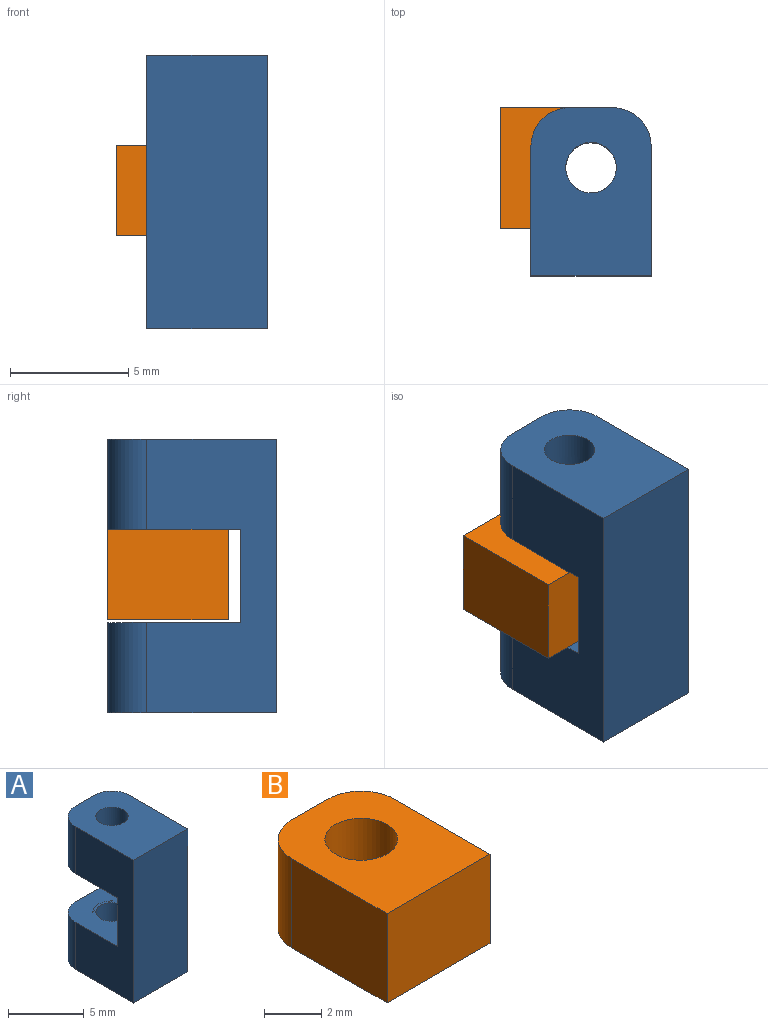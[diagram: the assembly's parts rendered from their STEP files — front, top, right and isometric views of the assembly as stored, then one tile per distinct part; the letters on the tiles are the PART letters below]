
ASSEMBLY  parts=2 mates=1
PART A: 17 faces, bbox 5.1x7.1x11.6 mm
  f0: plane 5.59x5.08mm, normal (0,0,-1), area 23.6mm2, adj f1,f2,f3,f4,f6,f7,f8
  f1: plane 11.56x5.46mm, normal (1,0,0), area 47.6mm2, adj f0,f2,f5,f8,f9,f11,f13,f16
  f2: cylinder r=1.65mm len=3.81mm, axis (0,0,-1), area 9.9mm2, adj f0,f1,f3,f5
  f3: plane 3.81x1.78mm, normal (0,1,0), area 6.8mm2, adj f0,f2,f4,f5
  f4: cylinder r=1.65mm len=3.81mm, axis (0,0,-1), area 9.9mm2, adj f0,f3,f5,f7
  f5: plane 7.11x5.08mm, normal (0,0,1), area 31.4mm2, adj f1,f2,f3,f4,f6,f7,f16
  f6: cylinder r=1.07mm len=3.81mm, axis (0,0,-1), area 25.5mm2, adj f0,f5
  f7: plane 11.56x5.46mm, normal (-1,0,0), area 47.6mm2, adj f0,f4,f5,f8,f9,f11,f12,f16
  f8: plane 5.08x3.94mm, normal (0,1,0), area 20mm2, adj f0,f1,f7,f9
  f9: plane 5.6x5.09mm, normal (0,0,1), area 23.3mm2, adj f1,f7,f8,f10,f12,f13,f14,f15
  f10: plane 3.81x1.78mm, normal (0,1,0), area 6.8mm2, adj f9,f11,f12,f13
  f11: plane 7.11x5.08mm, normal (0,0,-1), area 31.4mm2, adj f1,f7,f10,f12,f13,f14,f16
  f12: cylinder r=1.65mm len=3.81mm, axis (0,0,-1), area 9.9mm2, adj f7,f9,f10,f11
  f13: cylinder r=1.65mm len=3.81mm, axis (0,0,-1), area 9.9mm2, adj f1,f9,f10,f11
  f14: cylinder r=1.07mm len=3.81mm, axis (0,0,-1), area 25.5mm2, adj f9,f11,f15
  f15: plane 1.83x0.39mm, normal (0,-0.02,1), area 0.3mm2, adj f9,f14
  f16: plane 11.56x5.08mm, normal (0,-1,0), area 58.7mm2, adj f1,f5,f7,f11
PART B: 9 faces, bbox 5.1x6.4x3.8 mm
  f0: plane 3.81x1.78mm, normal (0,1,0), area 6.8mm2, adj f5,f6,f7,f8
  f1: plane 4.7x3.81mm, normal (-1,0,0), area 17.9mm2, adj f2,f5,f6,f7
  f2: plane 5.08x3.81mm, normal (0,-1,0), area 19.4mm2, adj f1,f4,f5,f6
  f3: cylinder r=1.27mm len=3.81mm, axis (0,0,-1), area 30.4mm2, adj f5,f6
  f4: plane 4.7x3.81mm, normal (1,0,0), area 17.9mm2, adj f2,f5,f6,f8
  f5: plane 6.35x5.08mm, normal (0,0,1), area 26mm2, adj f0,f1,f2,f3,f4,f7,f8
  f6: plane 6.35x5.08mm, normal (0,0,-1), area 26mm2, adj f0,f1,f2,f3,f4,f7,f8
  f7: cylinder r=1.65mm len=3.81mm, axis (0,0,-1), area 9.9mm2, adj f0,f1,f5,f6
  f8: cylinder r=1.65mm len=3.81mm, axis (0,0,-1), area 9.9mm2, adj f0,f4,f5,f6
PLACE A at identity
PLACE B rot(axis=(0,0,-1),90deg) t=(-67.4,-7.27,0.06)mm
MATE revolute B.f3 <-> A.f6  axis (0,0,1) through (-31.97,35.44,3.87)mm
